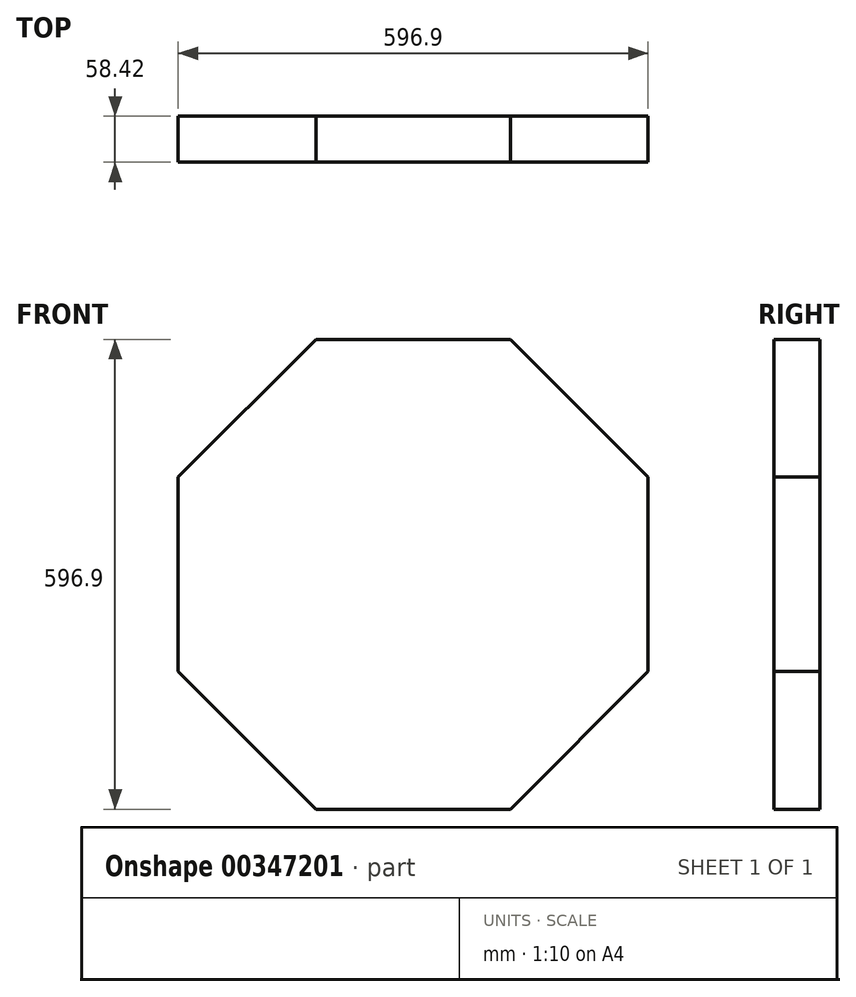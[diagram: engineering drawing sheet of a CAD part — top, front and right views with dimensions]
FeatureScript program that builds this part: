
annotation { "Feature Type Name" : "Feature", "Feature Type Description" : "" }
export const myFeature = defineFeature(function(context is Context, id is Id, definition is map)
    precondition{}
    {
        {
            var Q0;
            Q0=qCreatedBy(makeId("Front.planeOp"),FACE);
            var sketch = newSketch(context, id + "F0", { "sketchPlane" : qUnion([Q0])});
            skCircle(sketch, "E0.cCircle", {"center": v(13.04, 462.6) * mm, "radius": 298.45 * mm, "construction": true});
            skLineSegment(sketch, "E0.0", {"start": v(136.66, 164.16) * mm, "end": v(-110.58, 164.16) * mm});
            skLineSegment(sketch, "E0.1", {"start": v(-110.58, 164.16) * mm, "end": v(-285.4, 338.99) * mm});
            skLineSegment(sketch, "E0.2", {"start": v(-285.4, 338.99) * mm, "end": v(-285.4, 586.23) * mm});
            skLineSegment(sketch, "E0.3", {"start": v(-285.4, 586.23) * mm, "end": v(-110.58, 761.06) * mm});
            skLineSegment(sketch, "E0.4", {"start": v(-110.58, 761.06) * mm, "end": v(136.66, 761.06) * mm});
            skLineSegment(sketch, "E0.5", {"start": v(136.66, 761.06) * mm, "end": v(311.5, 586.23) * mm});
            skLineSegment(sketch, "E0.6", {"start": v(311.5, 586.23) * mm, "end": v(311.5, 338.99) * mm});
            skLineSegment(sketch, "E0.7", {"start": v(311.5, 338.99) * mm, "end": v(136.66, 164.16) * mm});
            skPoint(sketch, "E0.0.midPoint", {"position": v(13.04, 164.16) * mm});
            skSolve(sketch);
        }
        {
            var Q0;
            Q0=makeQuery(id+"F0.imprint","IMPRINT",FACE,{"disambiguationData":[TD([[makeQuery(id+"F0.imprint","IMPRINT",EDGE,{"derivedFrom":sQuery(id+"F0.wireOp",EDGE,"E0.0")}),-1.0]])]});
            extrude(context, id + "F1", {"entities" : qUnion([Q0]), "depth" : 58.42 * mm});
        }
    });
